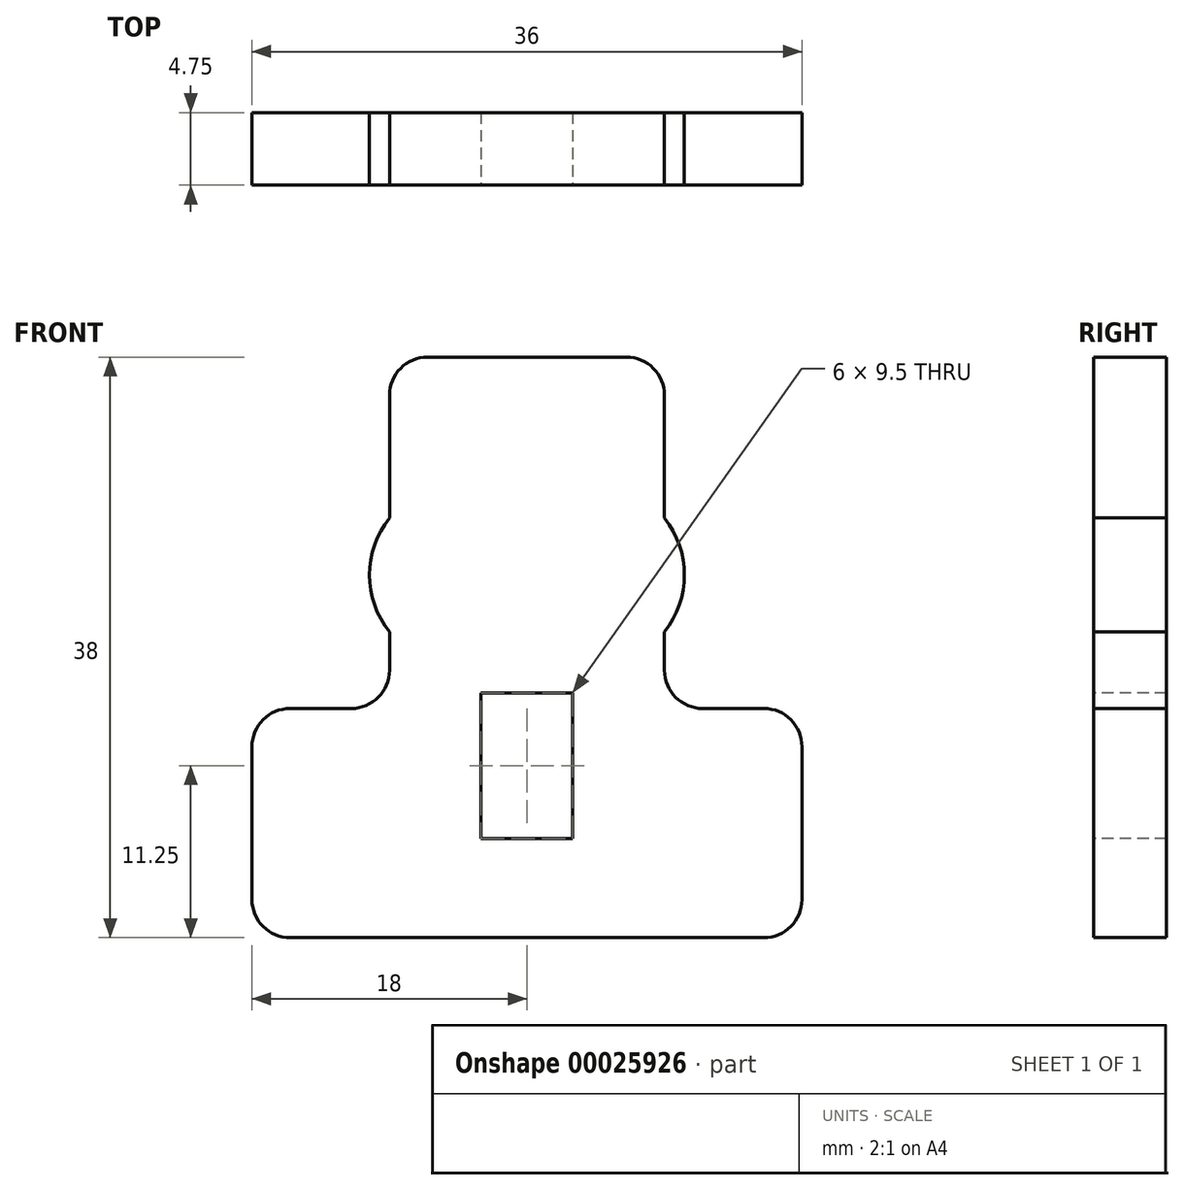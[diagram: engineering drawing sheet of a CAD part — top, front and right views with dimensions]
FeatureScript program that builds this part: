
annotation { "Feature Type Name" : "Feature", "Feature Type Description" : "" }
export const myFeature = defineFeature(function(context is Context, id is Id, definition is map)
    precondition{}
    {
        {
            var Q0;
            Q0=qCreatedBy(makeId("Front.planeOp"),FACE);
            var sketch = newSketch(context, id + "F0", { "sketchPlane" : qUnion([Q0])});
            skLineSegment(sketch, "E0", {"start": v(0, -15) * mm, "end": v(-18, -15) * mm});
            skLineSegment(sketch, "E1", {"start": v(-18, -15) * mm, "end": v(-18, 0) * mm});
            skLineSegment(sketch, "E2", {"start": v(-18, 0) * mm, "end": v(-9, 0) * mm});
            skLineSegment(sketch, "E3", {"start": v(-9, 0) * mm, "end": v(-9, 5) * mm});
            skLineSegment(sketch, "E4", {"start": v(-9, 23) * mm, "end": v(0, 23) * mm});
            skLineSegment(sketch, "E5.MirrorCS", {"start": v(9, 23) * mm, "end": v(0, 23) * mm});
            skLineSegment(sketch, "E6.MirrorCS", {"start": v(9, 0) * mm, "end": v(9, 5) * mm});
            skLineSegment(sketch, "E7.MirrorCS", {"start": v(18, 0) * mm, "end": v(9, 0) * mm});
            skLineSegment(sketch, "E8.MirrorCS", {"start": v(18, -15) * mm, "end": v(18, 0) * mm});
            skLineSegment(sketch, "E9.MirrorCS", {"start": v(0, -15) * mm, "end": v(18, -15) * mm});
            skLineSegment(sketch, "E10", {"start": v(0, 1) * mm, "end": v(-3, 1) * mm});
            skLineSegment(sketch, "E11", {"start": v(-3, 1) * mm, "end": v(-3, -8.5) * mm});
            skLineSegment(sketch, "E12", {"start": v(-3, -8.5) * mm, "end": v(0, -8.5) * mm});
            skLineSegment(sketch, "E13.MirrorCS", {"start": v(0, 1) * mm, "end": v(3, 1) * mm});
            skLineSegment(sketch, "E14.MirrorCS", {"start": v(3, 1) * mm, "end": v(3, -8.5) * mm});
            skLineSegment(sketch, "E15.MirrorCS", {"start": v(3, -8.5) * mm, "end": v(0, -8.5) * mm});
            skArc(sketch, "E16", {"start": v(-9, 12.47) * mm, "mid": v(-10.3, 8.73) * mm, "end": v(-9, 5) * mm});
            skArc(sketch, "E17.MirrorCS", {"start": v(9, 12.47) * mm, "mid": v(10.3, 8.73) * mm, "end": v(9, 5) * mm});
            skLineSegment(sketch, "E18.trimOffspring", {"start": v(-9, 12.47) * mm, "end": v(-9, 23) * mm});
            skLineSegment(sketch, "E19.trimOffspring", {"start": v(9, 12.47) * mm, "end": v(9, 23) * mm});
            skSolve(sketch);
        }
        {
            var Q0;
            Q0=makeQuery(id+"F0.imprint","IMPRINT",FACE,{"disambiguationData":[TD([[makeQuery(id+"F0.imprint","IMPRINT",EDGE,{"derivedFrom":sQuery(id+"F0.wireOp",EDGE,"E0")}),-1.0]])]});
            extrude(context, id + "F1", {"entities" : qUnion([Q0]), "oppositeDirection" : true, "depth" : 4.75 * mm});
        }
        {
            var Q0;
            Q0=makeQuery(id+"F1.opExtrude","SWEPT_EDGE",EDGE,{"disambiguationData":[OSD([sQuery(id+"F0.wireOp",EDGE,"E5.MirrorCS"),sQuery(id+"F0.wireOp",EDGE,"E19.trimOffspring")])]});
            var Q1;
            Q1=makeQuery(id+"F1.opExtrude","SWEPT_EDGE",EDGE,{"disambiguationData":[OSD([sQuery(id+"F0.wireOp",EDGE,"E6.MirrorCS"),sQuery(id+"F0.wireOp",EDGE,"E7.MirrorCS")])]});
            var Q2;
            Q2=makeQuery(id+"F1.opExtrude","SWEPT_EDGE",EDGE,{"disambiguationData":[OSD([sQuery(id+"F0.wireOp",EDGE,"E6.MirrorCS"),sQuery(id+"F0.wireOp",EDGE,"E7.MirrorCS")])]});
            var Q3;
            Q3=makeQuery(id+"F1.opExtrude","SWEPT_EDGE",EDGE,{"disambiguationData":[OSD([sQuery(id+"F0.wireOp",EDGE,"E7.MirrorCS"),sQuery(id+"F0.wireOp",EDGE,"E8.MirrorCS")])]});
            var Q4;
            Q4=makeQuery(id+"F1.opExtrude","SWEPT_EDGE",EDGE,{"disambiguationData":[OSD([sQuery(id+"F0.wireOp",EDGE,"E8.MirrorCS"),sQuery(id+"F0.wireOp",EDGE,"E9.MirrorCS")])]});
            var Q5;
            Q5=makeQuery(id+"F1.opExtrude","SWEPT_EDGE",EDGE,{"disambiguationData":[OSD([sQuery(id+"F0.wireOp",EDGE,"E2"),sQuery(id+"F0.wireOp",EDGE,"E3")])]});
            var Q6;
            Q6=makeQuery(id+"F1.opExtrude","SWEPT_EDGE",EDGE,{"disambiguationData":[OSD([sQuery(id+"F0.wireOp",EDGE,"E4"),sQuery(id+"F0.wireOp",EDGE,"E18.trimOffspring")])]});
            var Q7;
            Q7=makeQuery(id+"F1.opExtrude","SWEPT_EDGE",EDGE,{"disambiguationData":[OSD([sQuery(id+"F0.wireOp",EDGE,"E1"),sQuery(id+"F0.wireOp",EDGE,"E2")])]});
            var Q8;
            Q8=makeQuery(id+"F1.opExtrude","SWEPT_EDGE",EDGE,{"disambiguationData":[OSD([sQuery(id+"F0.wireOp",EDGE,"E0"),sQuery(id+"F0.wireOp",EDGE,"E1")])]});
            var Q9;
            Q9=makeQuery(id+"F1.opExtrude","SWEPT_EDGE",EDGE,{"disambiguationData":[OSD([sQuery(id+"F0.wireOp",EDGE,"E2"),sQuery(id+"F0.wireOp",EDGE,"E3")])]});
            fillet(context, id + "F2", {"entities" : qUnion([Q0, Q1, Q2, Q3, Q4, Q5, Q6, Q7, Q8, Q9]), "radius" : 2.5 * mm, "tangentPropagation" : true, "allowEdgeOverflow" : false});
        }
    });
